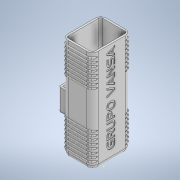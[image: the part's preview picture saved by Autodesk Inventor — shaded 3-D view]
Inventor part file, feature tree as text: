
AUTODESK INVENTOR PART (.ipt)
format: ipt  version: 2021 (Build 250183000, 183)  size: 1,768,448 bytes
history: native  units: mm
features: extrude x14, sketch x13, plane x7, mirror x6, fillet x6, projected_geometry x2, other x1
ambient origin geometry x8: Origin, YZ Plane, XZ Plane, XY Plane, X Axis, Y Axis, Z Axis, Center Point
bodies: Body1 (feature_tree)
feature tree (49):
  other  "Sólido1"
  extrude  "Extrusión1"  Depth=36.5mm
  extrude  "Extrusión2"  Depth=6.0mm
  extrude  "Extrusión3"  Depth=2.0mm
  plane  "Plano de trabajo1"
  mirror  "Simetría1"
  fillet  "Empalme1"  Radius=108.0mm
  plane  "Plano de trabajo2"
  extrude  "Extrusión4"  Depth=8.0mm
  plane  "Plano de trabajo3"
  mirror  "Simetría2"
  plane  "Plano de trabajo4"
  mirror  "Simetría3"
  plane  "Plano de trabajo5"
  mirror  "Simetría4"
  plane  "Plano de trabajo6"
  mirror  "Simetría5"
  plane  "Plano de trabajo8"
  mirror  "Simetría6"
  fillet  "Empalme2"  Radius=2.0mm
  fillet  "Empalme3"  Radius=2.0mm
  sketch  "Boceto4"  dims[d4=2.0mm d5=2.0mm d6=108.0mm d7=0.0mm]
  extrude  "Extrusión5"  Depth=2.0mm TaperAngle=0.0deg
  extrude  "Extrusión6"  Depth=6.0mm
  extrude  "Extrusión7"  Depth=11.0mm
  extrude  "Extrusión8"  [1 undecoded]
  extrude  "Extrusión9"  Depth=2.0mm
  fillet  "Empalme4"  Radius=2.0mm
  extrude  "Extrusión10"  [1 undecoded]
  extrude  "Extrusión11"  [1 undecoded]
  extrude  "Extrusión12"  Depth=1.0mm
  extrude  "Extrusión13"  Depth=9.0mm
  fillet  "Empalme6"  Radius=4.15mm
  extrude  "Extrusión14"  Depth=9.0mm
  fillet  "Empalme7"  Radius=24.0mm
  sketch  "Boceto2"  dims[d0=27.85mm d1=36.5mm]
  sketch  "Boceto3"  dims[d2=2.0mm d3=6.0mm]
  sketch  "Boceto5"  dims[d8=2.0mm d9=0.0mm d10=8.0mm d11=2.0mm d12=2.0mm]
  sketch  "Boceto6"  dims[d13=2.0mm d14=2.0mm d15=0.0mm]
  sketch  "Boceto7"  dims[d16=20.0mm d17=6.0mm]
  sketch  "Boceto8"  dims[d18=3.2mm d19=11.0mm]
  projected_geometry  "Contorno proyectado1"
  sketch  "Boceto9"  dims[d20=5.0mm d21=-4.0mm]
  sketch  "Boceto10"  dims[d22=0.8mm d23=5.0mm d24=2.0mm d25=0.0mm]
  sketch  "Boceto11"  dims[d26=-3.0mm d27=-4.0mm]
  sketch  "Boceto12"  dims[d28=-8.0mm d29=-33.5mm]
  sketch  "Boceto13"  dims[d30=1.0mm d31=1.0mm]
  projected_geometry  "Contorno proyectado2"
  sketch  "Boceto14"  dims[d32=0.5mm d33=0.0mm d37=20.0mm d38=4.15mm d39=4.35mm d40=24.0mm d41=14.0mm d42=0.0mm d43=8.0mm d44=0.0mm d45=7.0mm d46=2.0mm d47=15.0mm d48=0.0mm d49=2.0mm d50=7.0mm d51=0.0mm d52=2.0mm d53=6.0mm d54=0.0mm d56=14.0mm d57=0.0mm d58=8.0mm d59=0.0mm d60=8.0mm d61=0.0mm d62=2.0mm d63=8.0mm d64=0.0mm d65=75.0mm d66=75.0mm d67=16.5mm d68=11.273282mm d70=8.0mm d71=2.0mm d72=9.0mm d73=9.0mm d74=0.5mm d75=0.872665mm d76=0.5mm d77=0.872665mm]
note: 3 required parameter values undecoded (feature->parameter linkage not recoverable at this tier; creation-order binding heuristic only, values carry confidence <= 0.55)
